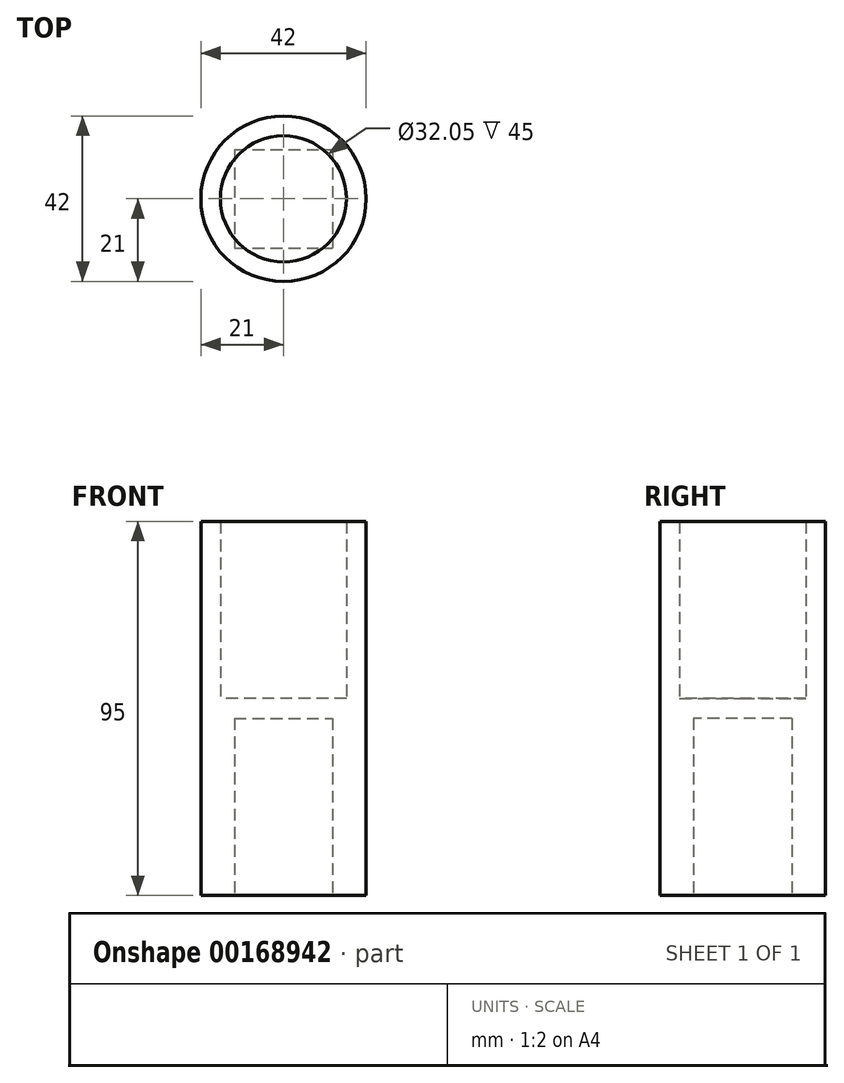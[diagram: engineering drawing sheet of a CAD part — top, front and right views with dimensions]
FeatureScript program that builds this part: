
annotation { "Feature Type Name" : "Feature", "Feature Type Description" : "" }
export const myFeature = defineFeature(function(context is Context, id is Id, definition is map)
    precondition{}
    {
        {
            var Q0;
            Q0=qCreatedBy(makeId("Top.planeOp"),FACE);
            var sketch = newSketch(context, id + "F0", { "sketchPlane" : qUnion([Q0])});
            skCircle(sketch, "E0", {"center": v(0, 0) * mm, "radius": 21 * mm});
            skLineSegment(sketch, "E1.bottom", {"start": v(-12.47, 12.47) * mm, "end": v(12.48, 12.47) * mm});
            skLineSegment(sketch, "E1.top", {"start": v(-12.48, -12.47) * mm, "end": v(12.47, -12.47) * mm});
            skLineSegment(sketch, "E1.left", {"start": v(-12.47, 12.47) * mm, "end": v(-12.48, -12.47) * mm});
            skLineSegment(sketch, "E1.right", {"start": v(12.48, 12.47) * mm, "end": v(12.47, -12.47) * mm});
            skSolve(sketch);
        }
        {
            var Q0;
            Q0=makeQuery(id+"F0.imprint","IMPRINT",FACE,{"disambiguationData":[TD([[makeQuery(id+"F0.imprint","IMPRINT",EDGE,{"derivedFrom":sQuery(id+"F0.wireOp",EDGE,"E0")}),1.0]])]});
            extrude(context, id + "F1", {"entities" : qUnion([Q0]), "depth" : 45 * mm});
        }
        {
            var Q0;
            Q0=makeQuery(id+"F1.opExtrude","CAP_FACE",FACE,{"disambiguationData":[OSD([sQuery(id+"F0.wireOp",EDGE,"E0"),sQuery(id+"F0.wireOp",EDGE,"E1.bottom"),sQuery(id+"F0.wireOp",EDGE,"E1.top"),sQuery(id+"F0.wireOp",EDGE,"E1.left"),sQuery(id+"F0.wireOp",EDGE,"E1.right")])],"isStart":false});
            var sketch = newSketch(context, id + "F2", { "sketchPlane" : qUnion([Q0])});
            skCircle(sketch, "E2", {"center": v(0, 0) * mm, "radius": 21 * mm});
            skCircle(sketch, "E3", {"center": v(0, 0) * mm, "radius": 16.02 * mm});
            skSolve(sketch);
        }
        {
            var Q0;
            Q0=makeQuery(id+"F2.imprint","IMPRINT",FACE,{"disambiguationData":[TD([[makeQuery(id+"F2.imprint","IMPRINT",EDGE,{"derivedFrom":sQuery(id+"F2.wireOp",EDGE,"E2")}),1.0]])]});
            var Q1;
            {var subQ0=sQuery(id+"F2.wireOp",EDGE,"E3");var subQ1=makeQuery(id+"F1.opExtrude","CAP_EDGE",EDGE,{"disambiguationData":[OSD([sQuery(id+"F0.wireOp",EDGE,"E1.top")])],"isStart":false});var subQ2=makeQuery(id+"F2.imprint","INTERSECT",VERTEX,{"disambiguationData":[OD(1.0)],"derivedFrom":[subQ1,subQ0]});Q1=makeQuery(id+"F2.imprint","IMPRINT",FACE,{"disambiguationData":[TD([[makeQuery(id+"F2.imprint","IMPRINT",EDGE,{"disambiguationData":[TD([[subQ2,-1.0]])],"derivedFrom":subQ0}),-1.0]])]});}
            var Q2;
            {var subQ0=sQuery(id+"F2.wireOp",EDGE,"E3");var subQ1=makeQuery(id+"F1.opExtrude","CAP_EDGE",EDGE,{"disambiguationData":[OSD([sQuery(id+"F0.wireOp",EDGE,"E1.left")])],"isStart":false});var subQ2=makeQuery(id+"F2.imprint","INTERSECT",VERTEX,{"disambiguationData":[OD(1.0)],"derivedFrom":[subQ1,subQ0]});Q2=makeQuery(id+"F2.imprint","IMPRINT",FACE,{"disambiguationData":[TD([[makeQuery(id+"F2.imprint","IMPRINT",EDGE,{"disambiguationData":[TD([[subQ2,-1.0]])],"derivedFrom":subQ0}),-1.0]])]});}
            var Q3;
            {var subQ0=sQuery(id+"F2.wireOp",EDGE,"E3");var subQ1=makeQuery(id+"F1.opExtrude","CAP_EDGE",EDGE,{"disambiguationData":[OSD([sQuery(id+"F0.wireOp",EDGE,"E1.bottom")])],"isStart":false});var subQ2=makeQuery(id+"F2.imprint","INTERSECT",VERTEX,{"disambiguationData":[OD(0.0)],"derivedFrom":[subQ1,subQ0]});Q3=makeQuery(id+"F2.imprint","IMPRINT",FACE,{"disambiguationData":[TD([[makeQuery(id+"F2.imprint","IMPRINT",EDGE,{"disambiguationData":[TD([[subQ2,1.0]])],"derivedFrom":subQ0}),-1.0]])]});}
            var Q4;
            {var subQ0=sQuery(id+"F2.wireOp",EDGE,"E3");var subQ1=makeQuery(id+"F1.opExtrude","CAP_EDGE",EDGE,{"disambiguationData":[OSD([sQuery(id+"F0.wireOp",EDGE,"E1.bottom")])],"isStart":false});var subQ2=makeQuery(id+"F2.imprint","INTERSECT",VERTEX,{"disambiguationData":[OD(1.0)],"derivedFrom":[subQ1,subQ0]});Q4=makeQuery(id+"F2.imprint","IMPRINT",FACE,{"disambiguationData":[TD([[makeQuery(id+"F2.imprint","IMPRINT",EDGE,{"disambiguationData":[TD([[subQ2,-1.0]])],"derivedFrom":subQ0}),-1.0]])]});}
            extrude(context, id + "F3", {"entities" : qUnion([Q0, Q1, Q2, Q3, Q4]), "operationType" : NewBodyOperationType.ADD, "depth" : 50 * mm});
        }
        {
            var Q0;
            {var subQ0=sQuery(id+"F2.wireOp",EDGE,"E3");var subQ1=makeQuery(id+"F1.opExtrude","CAP_EDGE",EDGE,{"disambiguationData":[OSD([sQuery(id+"F0.wireOp",EDGE,"E1.bottom")])],"isStart":false});var subQ2=makeQuery(id+"F2.imprint","INTERSECT",VERTEX,{"disambiguationData":[OD(0.0)],"derivedFrom":[subQ1,subQ0]});Q0=makeQuery(id+"F2.imprint","IMPRINT",FACE,{"disambiguationData":[TD([[makeQuery(id+"F2.imprint","IMPRINT",EDGE,{"disambiguationData":[TD([[subQ2,-1.0]])],"derivedFrom":subQ0}),1.0]])]});}
            var Q1;
            {var subQ0=sQuery(id+"F2.wireOp",EDGE,"E3");var subQ1=makeQuery(id+"F1.opExtrude","CAP_EDGE",EDGE,{"disambiguationData":[OSD([sQuery(id+"F0.wireOp",EDGE,"E1.right")])],"isStart":false});var subQ2=makeQuery(id+"F2.imprint","INTERSECT",VERTEX,{"disambiguationData":[OD(0.0)],"derivedFrom":[subQ1,subQ0]});Q1=makeQuery(id+"F2.imprint","IMPRINT",FACE,{"disambiguationData":[TD([[makeQuery(id+"F2.imprint","IMPRINT",EDGE,{"disambiguationData":[TD([[subQ2,1.0]])],"derivedFrom":subQ0}),1.0]])]});}
            var Q2;
            {var subQ0=sQuery(id+"F2.wireOp",EDGE,"E3");var subQ1=makeQuery(id+"F1.opExtrude","CAP_EDGE",EDGE,{"disambiguationData":[OSD([sQuery(id+"F0.wireOp",EDGE,"E1.left")])],"isStart":false});var subQ2=makeQuery(id+"F2.imprint","INTERSECT",VERTEX,{"disambiguationData":[OD(0.0)],"derivedFrom":[subQ1,subQ0]});Q2=makeQuery(id+"F2.imprint","IMPRINT",FACE,{"disambiguationData":[TD([[makeQuery(id+"F2.imprint","IMPRINT",EDGE,{"disambiguationData":[TD([[subQ2,-1.0]])],"derivedFrom":subQ0}),1.0]])]});}
            var Q3;
            {var subQ0=sQuery(id+"F2.wireOp",EDGE,"E3");var subQ1=makeQuery(id+"F1.opExtrude","CAP_EDGE",EDGE,{"disambiguationData":[OSD([sQuery(id+"F0.wireOp",EDGE,"E1.top")])],"isStart":false});var subQ2=makeQuery(id+"F2.imprint","INTERSECT",VERTEX,{"disambiguationData":[OD(0.0)],"derivedFrom":[subQ1,subQ0]});Q3=makeQuery(id+"F2.imprint","IMPRINT",FACE,{"disambiguationData":[TD([[makeQuery(id+"F2.imprint","IMPRINT",EDGE,{"disambiguationData":[TD([[subQ2,-1.0]])],"derivedFrom":subQ0}),1.0]])]});}
            var Q4;
            {var subQ0=sQuery(id+"F2.wireOp",EDGE,"E3");var subQ8=makeQuery(id+"F1.opExtrude","CAP_EDGE",EDGE,{"disambiguationData":[OSD([sQuery(id+"F0.wireOp",EDGE,"E1.bottom")])],"isStart":false});var subQ9=makeQuery(id+"F2.imprint","INTERSECT",VERTEX,{"disambiguationData":[OD(0.0)],"derivedFrom":[subQ8,subQ0]});Q4=makeQuery(id+"F2.imprint","IMPRINT",FACE,{"disambiguationData":[TD([[makeQuery(id+"F2.imprint","IMPRINT",EDGE,{"disambiguationData":[TD([[subQ9,1.0]])],"derivedFrom":subQ0}),1.0]])]});}
            extrude(context, id + "F4", {"entities" : qUnion([Q0, Q1, Q2, Q3, Q4]), "operationType" : NewBodyOperationType.ADD, "depth" : 5 * mm});
        }
    });
